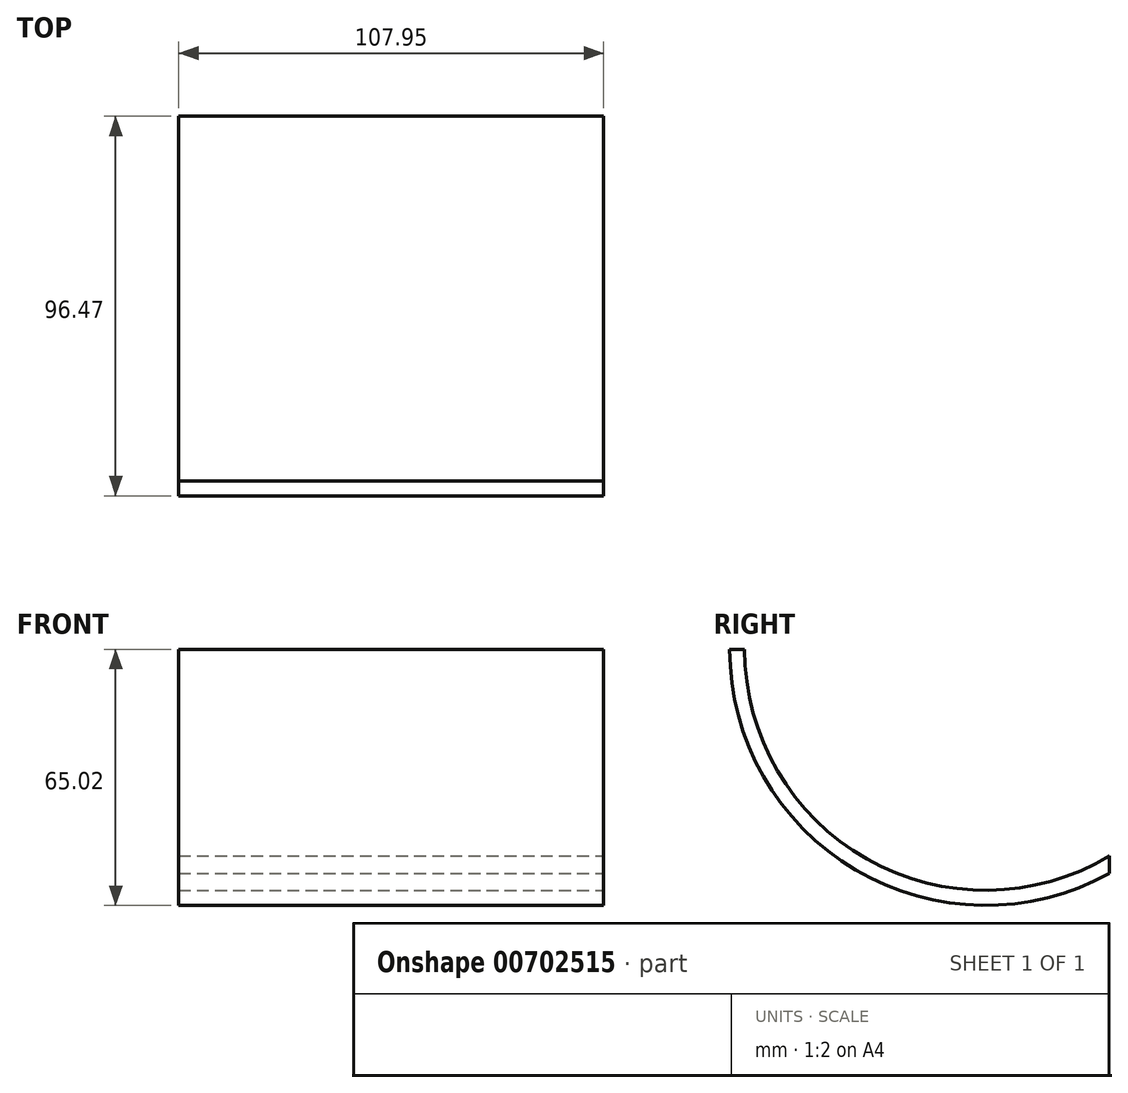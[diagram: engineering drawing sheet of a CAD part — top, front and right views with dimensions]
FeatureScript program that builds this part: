
annotation { "Feature Type Name" : "Feature", "Feature Type Description" : "" }
export const myFeature = defineFeature(function(context is Context, id is Id, definition is map)
    precondition{}
    {
        {
            var Q0;
            Q0=qCreatedBy(makeId("Right.planeOp"),FACE);
            var sketch = newSketch(context, id + "F0", { "sketchPlane" : qUnion([Q0])});
            skArc(sketch, "E0", {"start": v(-57.48, 0) * mm, "mid": v(-25.5, -56) * mm, "end": v(39, -56.91) * mm});
            skArc(sketch, "E1", {"start": v(-53.67, 0) * mm, "mid": v(-22.64, -53.26) * mm, "end": v(39, -52.52) * mm});
            skLineSegment(sketch, "E2", {"start": v(-57.48, 0) * mm, "end": v(-53.67, 0) * mm});
            skLineSegment(sketch, "E3", {"start": v(39, -52.52) * mm, "end": v(39, -56.91) * mm});
            skPoint(sketch, "E4.orphan", {"position": v(60.63, -30.48) * mm});
            skSolve(sketch);
        }
        {
            var Q0;
            Q0 = qSketchRegion(id + "F0", true);
            extrude(context, id + "F1", {"entities" : qUnion([Q0]), "oppositeDirection" : true, "depth" : 107.95 * mm, "offsetDistance" : 25.4 * mm});
        }
    });
